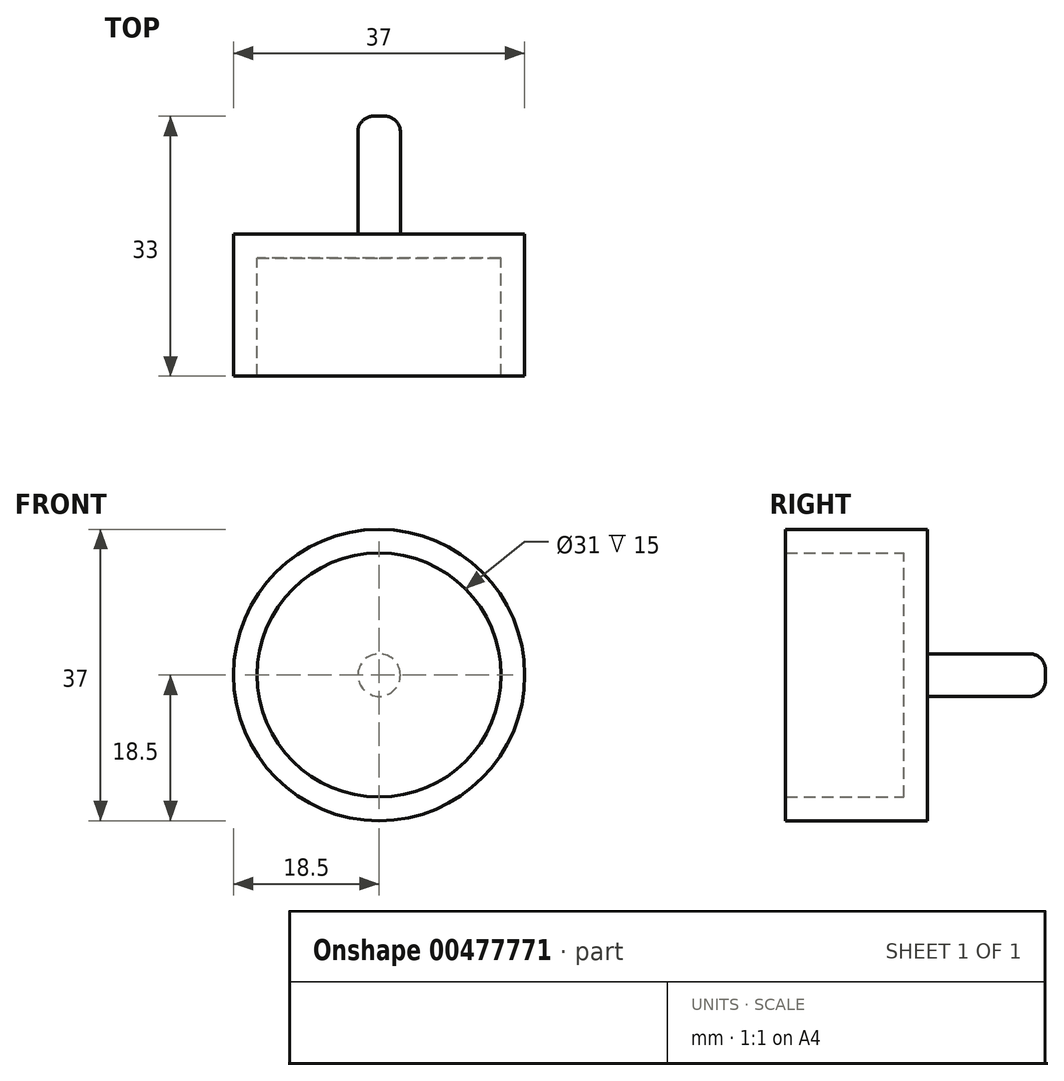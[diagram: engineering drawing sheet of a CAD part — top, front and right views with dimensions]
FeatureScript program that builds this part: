
annotation { "Feature Type Name" : "Feature", "Feature Type Description" : "" }
export const myFeature = defineFeature(function(context is Context, id is Id, definition is map)
    precondition{}
    {
        {
            var Q0;
            Q0=qCreatedBy(makeId("Front.planeOp"),FACE);
            var sketch = newSketch(context, id + "F0", { "sketchPlane" : qUnion([Q0])});
            skCircle(sketch, "E0", {"center": v(0, 0) * mm, "radius": 18.5 * mm});
            skSolve(sketch);
        }
        {
            var Q0;
            Q0 = qSketchRegion(id + "F0", true);
            extrude(context, id + "F1", {"entities" : qUnion([Q0]), "depth" : 18 * mm});
        }
        {
            var Q0;
            Q0=makeQuery(id+"F1.opExtrude","CAP_FACE",FACE,{"disambiguationData":[OSD([sQuery(id+"F0.wireOp",EDGE,"E0")])],"isStart":false});
            shell(context, id + "F2", {"entities" : qUnion([Q0]), "thickness" : 3 * mm});
        }
        {
            var Q0;
            Q0=makeQuery(id+"F1.opExtrude","CAP_FACE",FACE,{"disambiguationData":[OSD([sQuery(id+"F0.wireOp",EDGE,"E0")])],"isStart":true});
            var sketch = newSketch(context, id + "F3", { "sketchPlane" : qUnion([Q0])});
            skCircle(sketch, "E1", {"center": v(0, 0) * mm, "radius": 2.7 * mm});
            skSolve(sketch);
        }
        {
            var Q0;
            Q0=makeQuery(id+"F3.imprint","IMPRINT",FACE,{"disambiguationData":[TD([[makeQuery(id+"F3.imprint","IMPRINT",EDGE,{"derivedFrom":sQuery(id+"F3.wireOp",EDGE,"E1")}),1.0]])]});
            extrude(context, id + "F4", {"entities" : qUnion([Q0]), "operationType" : NewBodyOperationType.ADD, "depth" : 15 * mm});
        }
        {
            var Q0;
            Q0=makeQuery(id+"F4.opExtrude","CAP_EDGE",EDGE,{"disambiguationData":[OSD([sQuery(id+"F3.wireOp",EDGE,"E1")])],"isStart":false});
            fillet(context, id + "F5", {"entities" : qUnion([Q0]), "radius" : 2 * mm, "tangentPropagation" : true, "allowEdgeOverflow" : false});
        }
    });
